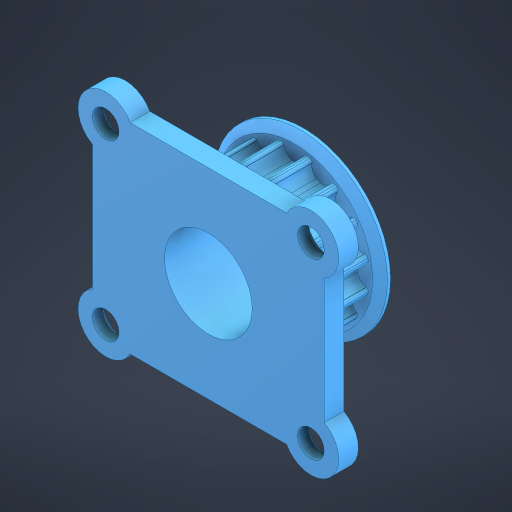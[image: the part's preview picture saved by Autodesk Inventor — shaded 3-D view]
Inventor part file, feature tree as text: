
AUTODESK INVENTOR PART (.ipt)
format: ipt  version: 2024.2 (Build 282272000, 272)  size: 510,976 bytes
history: native  units: in
note: dims shown in document units (in); Inventor stores cm internally (conversion verified against a paired STEP export)
features: extrude x4, sketch x3, other x2
ambient origin geometry x8: Origin, YZ Plane, XZ Plane, XY Plane, X Axis, Y Axis, Z Axis, Center Point
bodies: Solid1 (feature_tree)
feature tree (9):
  other  "HTD Pulley - 5mm.step"
  extrude  "Extrusion1"  Depth=0.1693in
  sketch  "Sketch2"  dims[d2=0.1693in d3=0.1693in]
  extrude  "Extrusion4"  Depth=0.1693in
  extrude  "Extrusion2"  TaperAngle=0.0deg  [1 undecoded]
  extrude  "Extrusion3"  TaperAngle=0.0deg  [1 undecoded]
  sketch  "Sketch1"  dims[d0=0.1693in d1=0.1693in]
  sketch  "Sketch3"  dims[d4=0.0in d5=0.0in d6=0.0in d7=0.0in d9=0.5545in d10=0.5545in d11=0.6545in d12=0.6545in d15=0.125in d16=0.0in d18=0.2953in d19=0.2953in d20=0.2953in d21=0.2953in d22=0.0591in d23=0.0in d24=0.5591in d25=0.0in d26=0.0in d33=0.3543in d34=0.3543in d35=0.3543in d36=0.3543in d37=0.0in d38=0.0in d39=0.0in d40=0.0in d41=0.0in]
  other  "Part 1"
note: 2 required parameter values undecoded (feature->parameter linkage not recoverable at this tier; creation-order binding heuristic only, values carry confidence <= 0.55)
